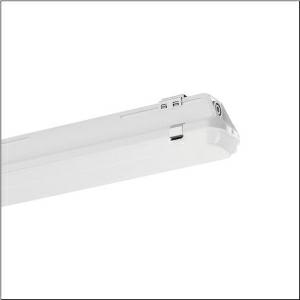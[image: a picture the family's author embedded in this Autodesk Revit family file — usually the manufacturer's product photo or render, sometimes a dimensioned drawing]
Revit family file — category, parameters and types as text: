
# Revit family: monsun_r__21_parking_51fg207l430k_4ecc
name_source: partatom
category: Lighting Fixtures
units: mm (PartAtom-declared; Revit-internal decimal feet)

## family parameters
Cut with Voids When Loaded = No
Host = Face
Light Source = No
Part Type = Normal
Room Calculation Point = No
Round Connector Dimension = Use Diameter
Shared = No

## types (1)
- Monsun® 21 parking (1 x LED, 3930 lm, 24.7 W, 4000K)
    Apparent Load = 25 VA
    CIE Flux Codes = 45 75 93 94 100
    Color Rendering = 80
    Color Temperature = 4000K
    Default Elevation = 1800 mm
    Description = Monsun® 21 parking, damp-proof luminaire, chain hanger, primary optical cover: enclosure, of PC, light emission: direct distribution, primary light characteristic: symmetric, installation type: suspended mounting, surface-mounted, horizontal mounting, vertical mounting, LED, rated luminous flux: 3.930lm, luminous efficacy: 159lm/W, light colour: 840, colour temperature: 4000K, control gear: ON/OFF, with terminal, 3-pole, max. 2.5mm², mains connection: 220..240V, AC, 50/60Hz, rated input power: 25W, housing, of glass-fibre reinforced plastic, uncoated, bright grey, incl. chain hanger, length: 1.299mm, width: 90mm, height: 88mm, clip for enclosure, of stainless steel (V2A), ceiling mounting element, of stainless steel (V2A), chain hanger, of stainless steel (V2A), protection rating (complete): IP66, insulation class (complete): insulation class I (protective earthing), certification: CE, ENEC, VDE, UKCA, protection symbol: D, impact resistance: IK08, permissible operating ambient temperature: -25..+35°C, standard: EN 50419, EN 60598-2-1, corresponds to IFS (International Featured Standards) requirements for safety and quality in the food industry, for indoor or canopied outdoor use, no direct snow, no direct sun, no direct rain, LABS conformity tested according to VDMA 24364:2018-05, contact your sales advisor before using the luminaires in applications with unclear chemical exposure, large temperature fluctuations or condensation-forming humidity, packaging unit: 1 piece
    Height = 88 mm
    Lamp = 1 x LED
    Lamp Light Flux = 3930 lm
    Lamp Power = 24.7 W
    Lamp count = 1
    Length = 1299 mm
    Luminous efficacy = 159 lm/W
    Manufacturer = Siteco
    ModVariant = No
    Model = 51FG207L430K
    Mounting Place = Ceiling
    Mounting Type = Surface mounted
    Number of Poles = 1
    OnlyDefault = Yes
    Power Factor = 1
    Product Name = Monsun® 21 parking
    Product group = damp-proof luminaire
    ProductGroupID = 301
    Protection Class = Protection class I
    Protection Degree = IP 66
    RLX_Detail_Level = 1
    RLX_Emergency_Light_Flux = 0 lm
    RLX_Emergency_Type = 0
    RLX_Emergency_Type_DB = No
    RlxData = <blob elided: 89605 chars, md5=9ee2515f>
    Socket = socket
    Standby Power = 0 W
    System Light Flux = 3930 lm
    System Power = 25 W
    Type Comments = Product without accessories
    Type Image = l_1319656.jpg
    URL = http://relux.com
    VarID = ---
    Voltage = 0 V
    Weight = 0.00 kg
    Width = 90 mm

## geometry (parser evidence)
native form markers: Blend x4, Sweep x15
no freeform markers — native parametric forms only
